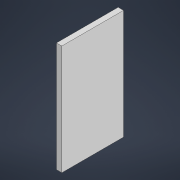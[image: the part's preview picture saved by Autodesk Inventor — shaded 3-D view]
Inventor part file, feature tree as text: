
AUTODESK INVENTOR PART (.ipt)
format: ipt  version: 2022 (Build 260153000, 153)  size: 84,992 bytes
history: native  units: mm
features: other x1, extrude x1, sketch x1
ambient origin geometry x8: Origin, YZ Plane, XZ Plane, XY Plane, X Axis, Y Axis, Z Axis, Center Point
bodies: Body1 (feature_tree)
feature tree (3):
  other  "Твердое тело1"
  extrude  "Выдавливание1"  Depth=450.0mm
  sketch  "Эскиз1"
